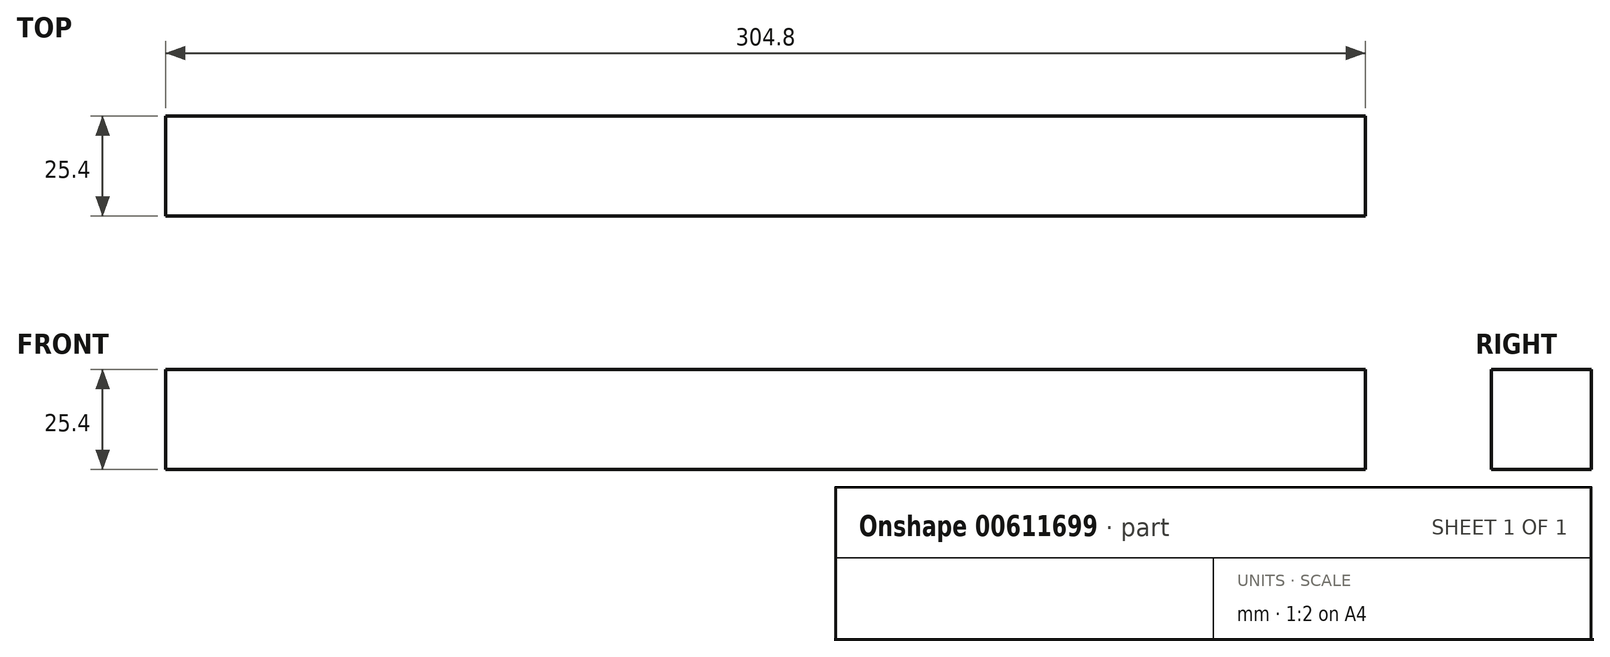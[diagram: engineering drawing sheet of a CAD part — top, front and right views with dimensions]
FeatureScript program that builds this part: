
annotation { "Feature Type Name" : "Feature", "Feature Type Description" : "" }
export const myFeature = defineFeature(function(context is Context, id is Id, definition is map)
    precondition{}
    {
        {
            var Q0;
            Q0=qCreatedBy(makeId("Right.planeOp"),FACE);
            var sketch = newSketch(context, id + "F0", { "sketchPlane" : qUnion([Q0])});
            skLineSegment(sketch, "E0.bottom", {"start": v(-12.7, 12.7) * mm, "end": v(12.7, 12.7) * mm});
            skLineSegment(sketch, "E0.top", {"start": v(-12.7, -12.7) * mm, "end": v(12.7, -12.7) * mm});
            skLineSegment(sketch, "E0.left", {"start": v(-12.7, 12.7) * mm, "end": v(-12.7, -12.7) * mm});
            skLineSegment(sketch, "E0.right", {"start": v(12.7, 12.7) * mm, "end": v(12.7, -12.7) * mm});
            skSolve(sketch);
        }
        {
            var Q0;
            Q0=makeQuery(id+"F0.imprint","IMPRINT",FACE,{"disambiguationData":[TD([[makeQuery(id+"F0.imprint","IMPRINT",EDGE,{"derivedFrom":sQuery(id+"F0.wireOp",EDGE,"E0.bottom")}),-1.0]])]});
            extrude(context, id + "F1", {"entities" : qUnion([Q0]), "depth" : 152.4 * mm, "offsetDistance" : 25.4 * mm, "hasSecondDirection" : true, "secondDirectionOppositeDirection" : true, "secondDirectionDepth" : 152.4 * mm});
        }
    });
